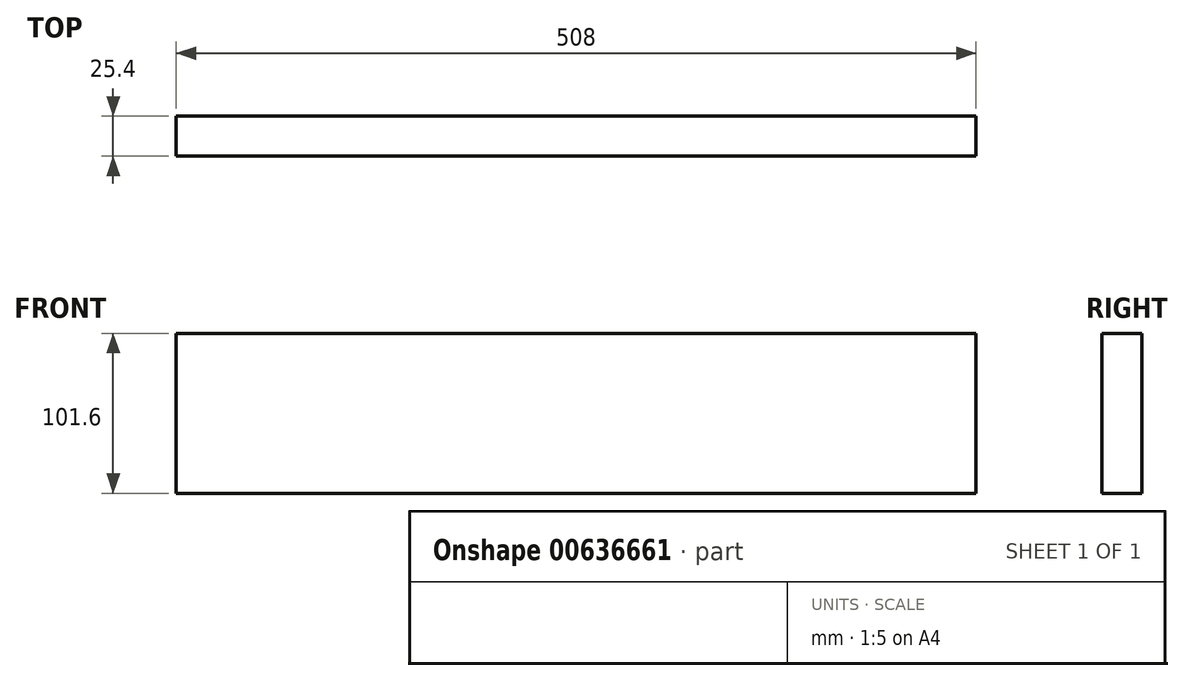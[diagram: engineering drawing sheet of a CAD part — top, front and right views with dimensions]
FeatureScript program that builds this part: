
annotation { "Feature Type Name" : "Feature", "Feature Type Description" : "" }
export const myFeature = defineFeature(function(context is Context, id is Id, definition is map)
    precondition{}
    {
        {
            var Q0;
            Q0=qCreatedBy(makeId("Front.planeOp"),FACE);
            var sketch = newSketch(context, id + "F0", { "sketchPlane" : qUnion([Q0])});
            skLineSegment(sketch, "E0.bottom", {"start": v(-52.2, 50.02) * mm, "end": v(455.8, 50.02) * mm});
            skLineSegment(sketch, "E0.top", {"start": v(-52.2, -51.58) * mm, "end": v(455.8, -51.58) * mm});
            skLineSegment(sketch, "E0.left", {"start": v(-52.2, 50.02) * mm, "end": v(-52.2, -51.58) * mm});
            skLineSegment(sketch, "E0.right", {"start": v(455.8, 50.02) * mm, "end": v(455.8, -51.58) * mm});
            skSolve(sketch);
        }
        {
            var Q0;
            Q0 = qSketchRegion(id + "F0", true);
            extrude(context, id + "F1", {"entities" : qUnion([Q0]), "depth" : 25.4 * mm, "offsetDistance" : 25.4 * mm});
        }
    });
